# Revit family: xSlide_Bar-American_Standard-Standard-1660_Series
name_source: partatom
category: Specialty Equipment
revit_build: Autodesk Revit 2014 (Build: 20130308_1515(x64)
units: mm (PartAtom-declared; Revit-internal decimal feet)

## types (2) — shared parameters
Assembly Code = C1030200
Finish = Brass-American Standard-002-Polished Chrome
Installation Type = Wall Mounted
Length = 2 1/2"
Manufacturer = American Standard
Material = Brass-American Standard-002-Polished Chrome
Price = Prices may vary. Please consult Manufacturer Representative for most up-to-date price list.
Product Documentation Link = https://www.americanstandard-us.com
Product Page URL = https://www.americanstandard-us.com
URL = https://www.americanstandard-us.com
Warranty Information = One Year General Product Warranty
Width = 5"

## per-type parameters (varying)
| type | Default Elevation | Description | Height |
| 1660.225 | 53" | 24" Standard Slide Bar | 24" |
| 1660.236 | 47" | 36" Standard Slide Bar | 36" |

note: column(s) folded — value = type name in every type: Model

## geometry (parser evidence)
native form markers: Sweep x3
no freeform markers — native parametric forms only
